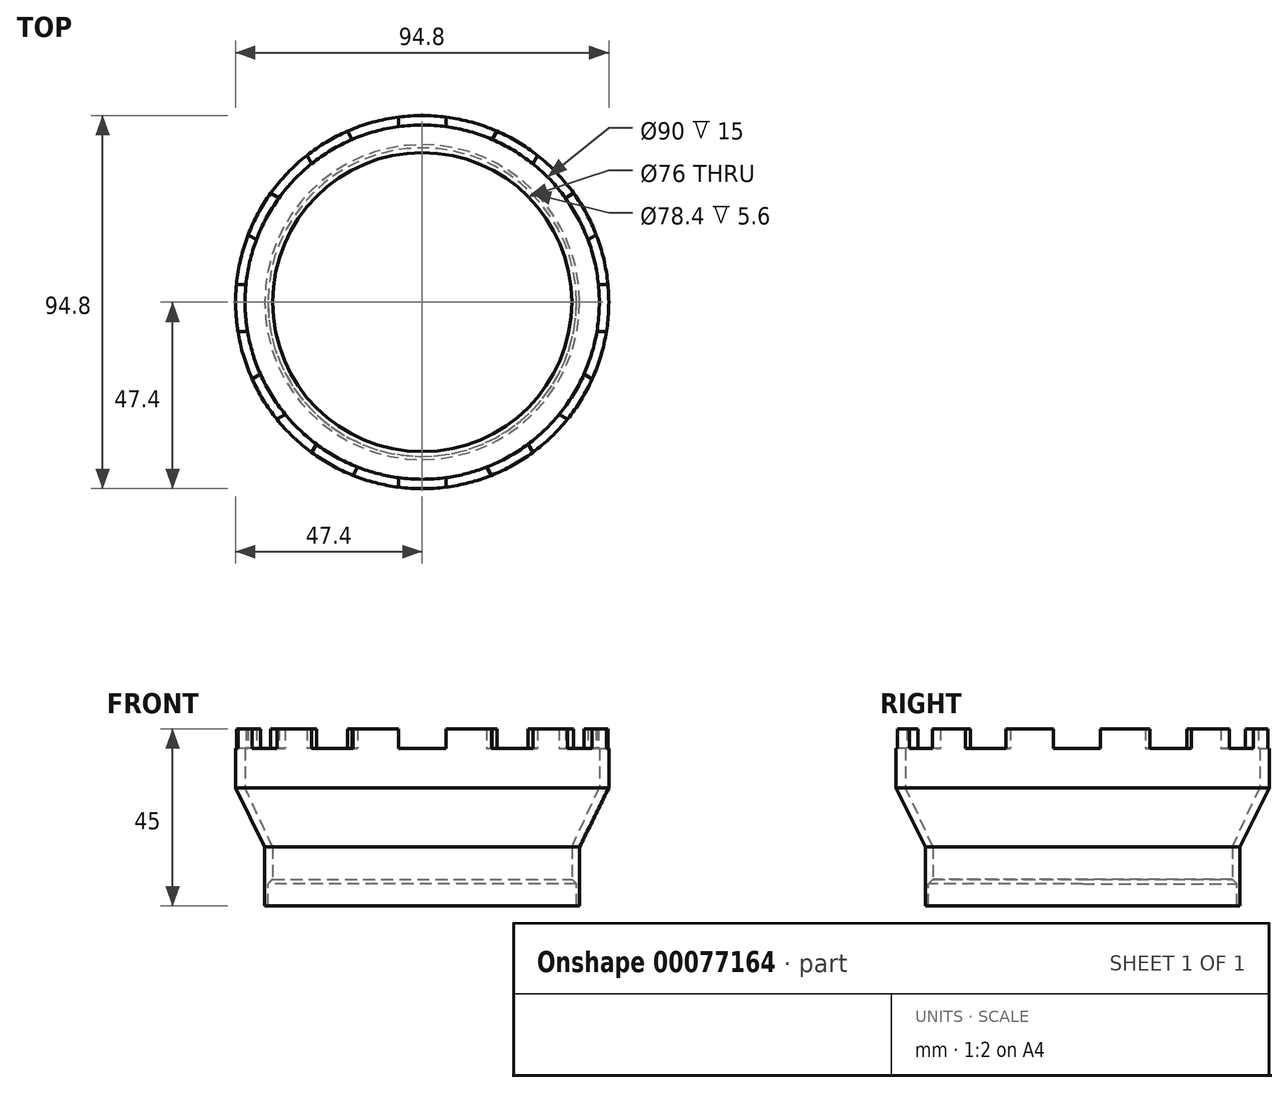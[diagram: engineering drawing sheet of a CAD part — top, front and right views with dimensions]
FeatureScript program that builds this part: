
annotation { "Feature Type Name" : "Feature", "Feature Type Description" : "" }
export const myFeature = defineFeature(function(context is Context, id is Id, definition is map)
    precondition{}
    {
        {
            var Q0;
            Q0=qCreatedBy(makeId("Top.planeOp"),FACE);
            var sketch = newSketch(context, id + "F0", { "sketchPlane" : qUnion([Q0])});
            skCircle(sketch, "E0", {"center": v(0, 0) * mm, "radius": 40 * mm});
            skCircle(sketch, "E1", {"center": v(0, 0) * mm, "radius": 38 * mm});
            skLineSegment(sketch, "E2", {"start": v(38, 0) * mm, "end": v(40, 0) * mm});
            skSolve(sketch);
        }
        {
            var Q0;
            Q0=qSketchRegion(id+"F0",true);
            extrude(context, id + "F1", {"entities" : qUnion([Q0]), "depth" : 15 * mm});
        }
        {
            var Q0;
            Q0=qCreatedBy(makeId("Front.planeOp"),FACE);
            var sketch = newSketch(context, id + "F2", { "sketchPlane" : qUnion([Q0])});
            skLineSegment(sketch, "E3", {"start": v(0, 0) * mm, "end": v(0, 30) * mm, "construction": true});
            skLineSegment(sketch, "E4", {"start": v(0, 0) * mm, "end": v(39.2, 0) * mm, "construction": true});
            skLineSegment(sketch, "E5.bottom", {"start": v(39.2, 0) * mm, "end": v(37.2, 0) * mm});
            skLineSegment(sketch, "E5.top", {"start": v(39.2, 5.6) * mm, "end": v(37.2, 5.6) * mm});
            skLineSegment(sketch, "E5.left", {"start": v(39.2, 0) * mm, "end": v(39.2, 5.6) * mm});
            skLineSegment(sketch, "E5.right", {"start": v(37.2, 0) * mm, "end": v(37.2, 5.6) * mm});
            skLineSegment(sketch, "E6", {"start": v(0, 15) * mm, "end": v(38, 15) * mm, "construction": true});
            skLineSegment(sketch, "E7", {"start": v(38, 15) * mm, "end": v(40, 15) * mm});
            skLineSegment(sketch, "E8", {"start": v(40, 15) * mm, "end": v(47.4, 30) * mm});
            skLineSegment(sketch, "E9", {"start": v(47.4, 30) * mm, "end": v(47.4, 45) * mm});
            skLineSegment(sketch, "E10", {"start": v(47.4, 45) * mm, "end": v(45, 45) * mm});
            skLineSegment(sketch, "E11", {"start": v(45, 45) * mm, "end": v(45, 30) * mm});
            skLineSegment(sketch, "E12", {"start": v(45, 30) * mm, "end": v(38, 15) * mm});
            skLineSegment(sketch, "E13", {"start": v(0, 30) * mm, "end": v(45, 30) * mm, "construction": true});
            skSolve(sketch);
        }
        {
            var Q0;
            Q0=qSketchRegion(id+"F2",true);
            var Q1;
            Q1=sQuery(id+"F2.wireOp",EDGE,"E3");
            revolve(context, id + "F3", {"operationType" : NewBodyOperationType.REMOVE, "entities" : qUnion([Q0]), "axis" : qUnion([Q1]), "revolveType" : RevolveType.FULL, "oppositeDirection" : true});
        }
        {
            var Q0;
            Q0=makeQuery(id+"F2.imprint","IMPRINT",FACE,{"disambiguationData":[TD([[makeQuery(id+"F2.imprint","IMPRINT",EDGE,{"derivedFrom":sQuery(id+"F2.wireOp",EDGE,"E7")}),1.0]])]});
            var Q1;
            Q1=sQuery(id+"F2.wireOp",EDGE,"E3");
            revolve(context, id + "F4", {"operationType" : NewBodyOperationType.ADD, "entities" : qUnion([Q0]), "axis" : qUnion([Q1]), "revolveType" : RevolveType.FULL});
        }
        {
            var Q0;
            Q0=makeQuery(id+"F4.opRevolve","SWEPT_FACE",FACE,{"disambiguationData":[OSD([sQuery(id+"F2.wireOp",EDGE,"E10")])]});
            var sketch = newSketch(context, id + "F5", { "sketchPlane" : qUnion([Q0])});
            skLineSegment(sketch, "E14", {"start": v(0, 0) * mm, "end": v(0, 46) * mm, "construction": true});
            skLineSegment(sketch, "E15.rect.bottom", {"start": v(6, 40) * mm, "end": v(-6, 40) * mm});
            skLineSegment(sketch, "E15.rect.top", {"start": v(6, 52) * mm, "end": v(-6, 52) * mm});
            skLineSegment(sketch, "E15.rect.left", {"start": v(6, 40) * mm, "end": v(6, 52) * mm});
            skLineSegment(sketch, "E15.rect.right", {"start": v(-6, 40) * mm, "end": v(-6, 52) * mm});
            skPoint(sketch, "E15.rect.middle", {"position": v(0, 46) * mm});
            skLineSegment(sketch, "E16.1.0", {"start": v(-21.55, 47.83) * mm, "end": v(-31.95, 41.83) * mm});
            skLineSegment(sketch, "E16.1.1", {"start": v(-15.55, 37.44) * mm, "end": v(-21.55, 47.83) * mm});
            skLineSegment(sketch, "E16.1.2", {"start": v(-15.55, 37.44) * mm, "end": v(-25.95, 31.44) * mm});
            skLineSegment(sketch, "E16.1.3", {"start": v(-25.95, 31.44) * mm, "end": v(-31.95, 41.83) * mm});
            skLineSegment(sketch, "E16.2.0", {"start": v(-43.33, 30.45) * mm, "end": v(-49.33, 20.05) * mm});
            skLineSegment(sketch, "E16.2.1", {"start": v(-32.94, 24.45) * mm, "end": v(-43.33, 30.45) * mm});
            skLineSegment(sketch, "E16.2.2", {"start": v(-32.94, 24.45) * mm, "end": v(-38.94, 14.05) * mm});
            skLineSegment(sketch, "E16.2.3", {"start": v(-38.94, 14.05) * mm, "end": v(-49.33, 20.05) * mm});
            skPoint(sketch, "E16.center", {"position": v(0, -1.5) * mm});
            skLineSegment(sketch, "E17.2.3.0", {"start": v(-53.5, 4.5) * mm, "end": v(-53.5, -7.5) * mm});
            skLineSegment(sketch, "E17.3.3.0", {"start": v(-41.5, 4.5) * mm, "end": v(-53.5, 4.5) * mm});
            skLineSegment(sketch, "E17.6.3.0", {"start": v(-41.5, 4.5) * mm, "end": v(-41.5, -7.5) * mm});
            skLineSegment(sketch, "E17.9.3.0", {"start": v(-41.5, -7.5) * mm, "end": v(-53.5, -7.5) * mm});
            skLineSegment(sketch, "E17.2.4.0", {"start": v(-49.33, -23.05) * mm, "end": v(-43.33, -33.45) * mm});
            skLineSegment(sketch, "E17.3.4.0", {"start": v(-38.94, -17.05) * mm, "end": v(-49.33, -23.05) * mm});
            skLineSegment(sketch, "E17.6.4.0", {"start": v(-38.94, -17.05) * mm, "end": v(-32.94, -27.45) * mm});
            skLineSegment(sketch, "E17.9.4.0", {"start": v(-32.94, -27.45) * mm, "end": v(-43.33, -33.45) * mm});
            skLineSegment(sketch, "E17.2.5.0", {"start": v(-31.95, -44.83) * mm, "end": v(-21.55, -50.83) * mm});
            skLineSegment(sketch, "E17.3.5.0", {"start": v(-25.95, -34.44) * mm, "end": v(-31.95, -44.83) * mm});
            skLineSegment(sketch, "E17.6.5.0", {"start": v(-25.95, -34.44) * mm, "end": v(-15.55, -40.44) * mm});
            skLineSegment(sketch, "E17.9.5.0", {"start": v(-15.55, -40.44) * mm, "end": v(-21.55, -50.83) * mm});
            skLineSegment(sketch, "E17.2.6.0", {"start": v(-6, -55) * mm, "end": v(6, -55) * mm});
            skLineSegment(sketch, "E17.3.6.0", {"start": v(-6, -43) * mm, "end": v(-6, -55) * mm});
            skLineSegment(sketch, "E17.6.6.0", {"start": v(-6, -43) * mm, "end": v(6, -43) * mm});
            skLineSegment(sketch, "E17.9.6.0", {"start": v(6, -43) * mm, "end": v(6, -55) * mm});
            skLineSegment(sketch, "E17.2.7.0", {"start": v(21.55, -50.83) * mm, "end": v(31.95, -44.83) * mm});
            skLineSegment(sketch, "E17.3.7.0", {"start": v(15.55, -40.44) * mm, "end": v(21.55, -50.83) * mm});
            skLineSegment(sketch, "E17.6.7.0", {"start": v(15.55, -40.44) * mm, "end": v(25.95, -34.44) * mm});
            skLineSegment(sketch, "E17.9.7.0", {"start": v(25.95, -34.44) * mm, "end": v(31.95, -44.83) * mm});
            skLineSegment(sketch, "E17.2.8.0", {"start": v(43.33, -33.45) * mm, "end": v(49.33, -23.05) * mm});
            skLineSegment(sketch, "E17.3.8.0", {"start": v(32.94, -27.45) * mm, "end": v(43.33, -33.45) * mm});
            skLineSegment(sketch, "E17.6.8.0", {"start": v(32.94, -27.45) * mm, "end": v(38.94, -17.05) * mm});
            skLineSegment(sketch, "E17.9.8.0", {"start": v(38.94, -17.05) * mm, "end": v(49.33, -23.05) * mm});
            skLineSegment(sketch, "E17.2.9.0", {"start": v(53.5, -7.5) * mm, "end": v(53.5, 4.5) * mm});
            skLineSegment(sketch, "E17.3.9.0", {"start": v(41.5, -7.5) * mm, "end": v(53.5, -7.5) * mm});
            skLineSegment(sketch, "E17.6.9.0", {"start": v(41.5, -7.5) * mm, "end": v(41.5, 4.5) * mm});
            skLineSegment(sketch, "E17.9.9.0", {"start": v(41.5, 4.5) * mm, "end": v(53.5, 4.5) * mm});
            skLineSegment(sketch, "E17.2.10.0", {"start": v(49.33, 20.05) * mm, "end": v(43.33, 30.45) * mm});
            skLineSegment(sketch, "E17.3.10.0", {"start": v(38.94, 14.05) * mm, "end": v(49.33, 20.05) * mm});
            skLineSegment(sketch, "E17.6.10.0", {"start": v(38.94, 14.05) * mm, "end": v(32.94, 24.45) * mm});
            skLineSegment(sketch, "E17.9.10.0", {"start": v(32.94, 24.45) * mm, "end": v(43.33, 30.45) * mm});
            skLineSegment(sketch, "E17.2.11.0", {"start": v(31.95, 41.83) * mm, "end": v(21.55, 47.83) * mm});
            skLineSegment(sketch, "E17.3.11.0", {"start": v(25.95, 31.44) * mm, "end": v(31.95, 41.83) * mm});
            skLineSegment(sketch, "E17.6.11.0", {"start": v(25.95, 31.44) * mm, "end": v(15.55, 37.44) * mm});
            skLineSegment(sketch, "E17.9.11.0", {"start": v(15.55, 37.44) * mm, "end": v(21.55, 47.83) * mm});
            skSolve(sketch);
        }
        {
            var Q0;
            Q0=qSketchRegion(id+"F5",true);
            extrude(context, id + "F6", {"entities" : qUnion([Q0]), "operationType" : NewBodyOperationType.REMOVE, "oppositeDirection" : true, "depth" : 5 * mm});
        }
        {
            var Q0;
            Q0=makeQuery(id+"F3.boolean.opBoolean","INTERSECT",EDGE,{"derivedFrom":[makeQuery(id+"F1.opExtrude","SWEPT_FACE",FACE,{"disambiguationData":[OSD([sQuery(id+"F0.wireOp",EDGE,"E1")])]}),makeQuery(id+"F3.opRevolve","SWEPT_FACE",FACE,{"disambiguationData":[OSD([sQuery(id+"F2.wireOp",EDGE,"E5.top")])]})]});
            chamfer(context, id + "F7", {"entities" : qUnion([Q0]), "width" : 1.2 * mm, "tangentPropagation" : true});
        }
    });
